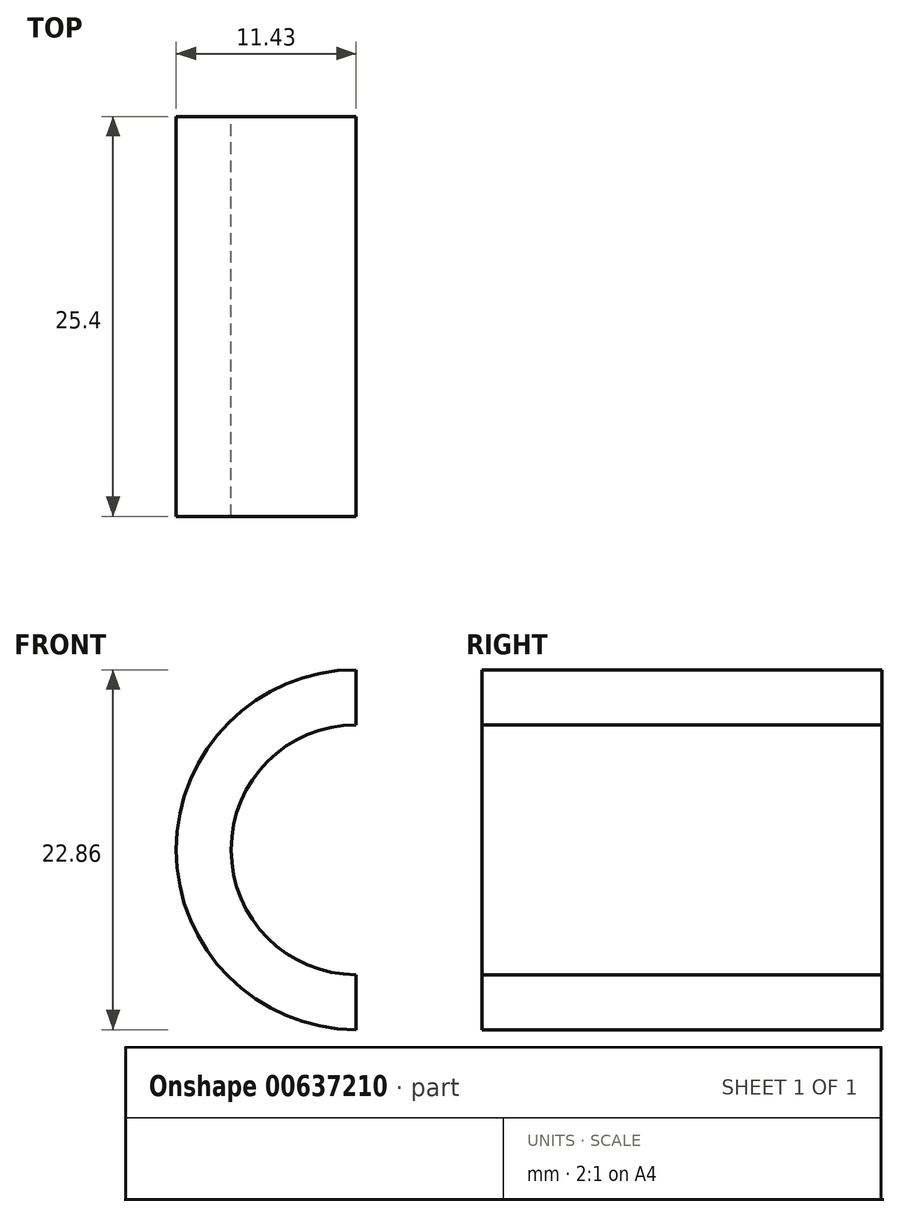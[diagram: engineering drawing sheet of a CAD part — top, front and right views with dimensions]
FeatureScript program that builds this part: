
annotation { "Feature Type Name" : "Feature", "Feature Type Description" : "" }
export const myFeature = defineFeature(function(context is Context, id is Id, definition is map)
    precondition{}
    {
        {
            var Q0;
            Q0=qCreatedBy(makeId("Front.planeOp"),FACE);
            var sketch = newSketch(context, id + "F0", { "sketchPlane" : qUnion([Q0])});
            skArc(sketch, "E0", {"start": v(0, 7.94) * mm, "mid": v(-7.94, 0) * mm, "end": v(0, -7.94) * mm});
            skArc(sketch, "E1", {"start": v(0, 11.43) * mm, "mid": v(-11.43, 0) * mm, "end": v(0, -11.43) * mm});
            skLineSegment(sketch, "E2", {"start": v(0, 0) * mm, "end": v(0, 11.43) * mm});
            skLineSegment(sketch, "E3", {"start": v(0, 11.43) * mm, "end": v(0, 7.94) * mm});
            skLineSegment(sketch, "E4", {"start": v(0, -7.94) * mm, "end": v(0, -11.43) * mm});
            skSolve(sketch);
        }
        {
            var Q0;
            Q0=makeQuery(id+"F0.imprint","IMPRINT",FACE,{"disambiguationData":[TD([[makeQuery(id+"F0.imprint","IMPRINT",EDGE,{"derivedFrom":sQuery(id+"F0.wireOp",EDGE,"E0")}),-1.0]])]});
            extrude(context, id + "F1", {"entities" : qUnion([Q0]), "depth" : 25.4 * mm, "offsetDistance" : 25.4 * mm});
        }
    });
